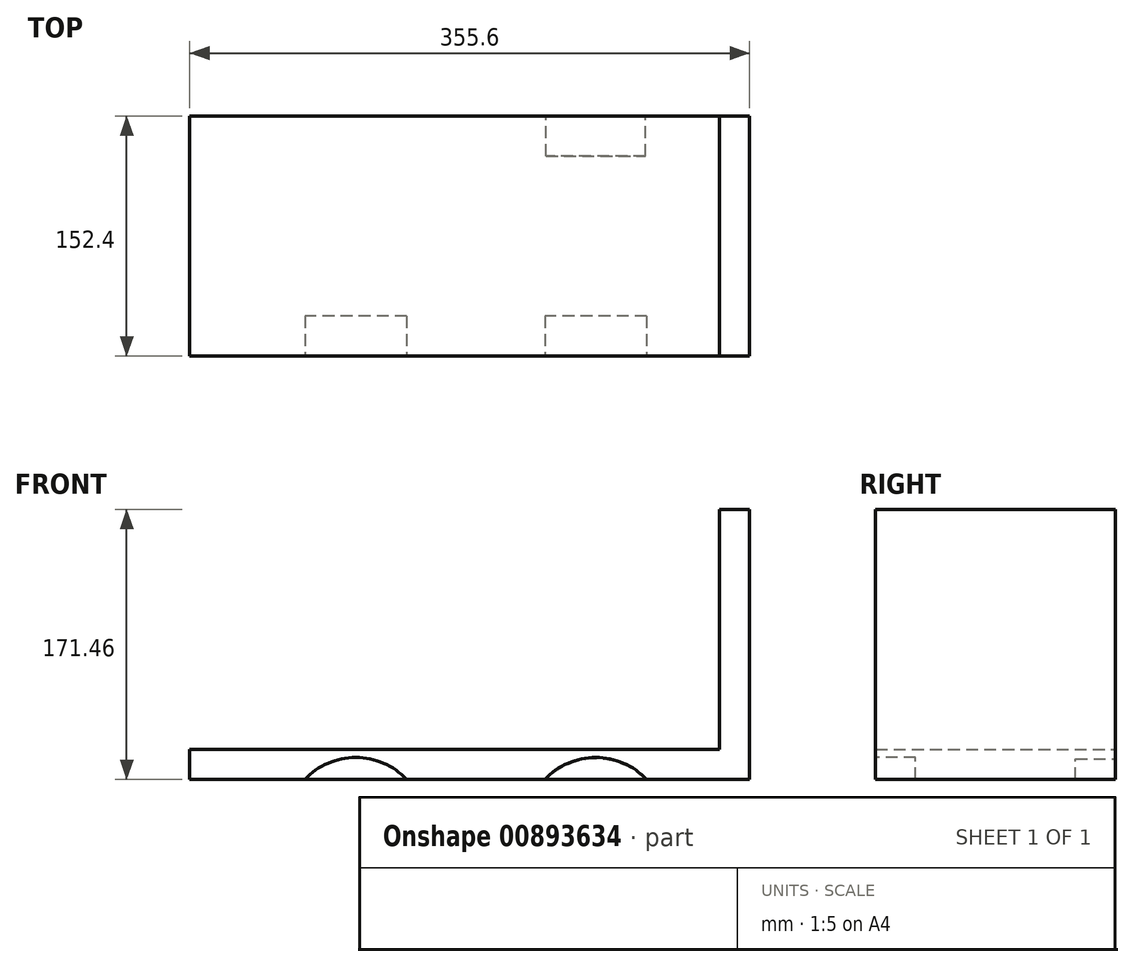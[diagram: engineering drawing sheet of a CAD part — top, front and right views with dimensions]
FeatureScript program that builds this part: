
annotation { "Feature Type Name" : "Feature", "Feature Type Description" : "" }
export const myFeature = defineFeature(function(context is Context, id is Id, definition is map)
    precondition{}
    {
        {
            var Q0;
            Q0=qCreatedBy(makeId("Front.planeOp"),FACE);
            var sketch = newSketch(context, id + "F0", { "sketchPlane" : qUnion([Q0])});
            skLineSegment(sketch, "E0.bottom", {"start": v(177.8, -9.52) * mm, "end": v(-177.8, -9.53) * mm});
            skLineSegment(sketch, "E0.top", {"start": v(177.8, 9.53) * mm, "end": v(-177.8, 9.53) * mm});
            skLineSegment(sketch, "E0.left", {"start": v(177.8, -9.52) * mm, "end": v(177.8, 9.53) * mm});
            skLineSegment(sketch, "E0.right", {"start": v(-177.8, -9.53) * mm, "end": v(-177.8, 9.53) * mm});
            skPoint(sketch, "E0.middle", {"position": v(0, 0) * mm});
            skPoint(sketch, "E1.middle", {"position": v(177.8, 9.53) * mm});
            skLineSegment(sketch, "E2", {"start": v(177.8, 9.53) * mm, "end": v(177.8, 161.93) * mm});
            skLineSegment(sketch, "E3", {"start": v(177.8, 161.93) * mm, "end": v(158.75, 161.93) * mm});
            skLineSegment(sketch, "E4", {"start": v(158.75, 161.93) * mm, "end": v(158.75, 9.53) * mm});
            skSolve(sketch);
        }
        {
            var Q0;
            Q0=makeQuery(id+"F0.imprint","IMPRINT",FACE,{"disambiguationData":[TD([[makeQuery(id+"F0.imprint","IMPRINT",EDGE,{"derivedFrom":sQuery(id+"F0.wireOp",EDGE,"E0.bottom")}),-1.0]])]});
            var Q1;
            {var subQ0=sQuery(id+"F0.wireOp",EDGE,"E2");Q1=makeQuery(id+"F0.imprint","IMPRINT",FACE,{"disambiguationData":[TD([[makeQuery(id+"F0.imprint","IMPRINT",EDGE,{"derivedFrom":subQ0}),1.0]])]});}
            extrude(context, id + "F1", {"entities" : qUnion([Q0, Q1]), "endBound" : BoundingType.SYMMETRIC, "depth" : 152.4 * mm, "offsetDistance" : 25.4 * mm});
        }
        {
            var Q0;
            Q0=makeQuery(id+"F1.opExtrude","CAP_FACE",FACE,{"disambiguationData":[OSD([sQuery(id+"F0.wireOp",EDGE,"E0.bottom"),sQuery(id+"F0.wireOp",EDGE,"E0.top"),sQuery(id+"F0.wireOp",EDGE,"E0.left"),sQuery(id+"F0.wireOp",EDGE,"E0.right"),sQuery(id+"F0.wireOp",EDGE,"E2"),sQuery(id+"F0.wireOp",EDGE,"E3"),sQuery(id+"F0.wireOp",EDGE,"E4")])],"isStart":false});
            var sketch = newSketch(context, id + "F2", { "sketchPlane" : qUnion([Q0])});
            skLineSegment(sketch, "E5", {"start": v(-177.8, -9.52) * mm, "end": v(-72.4, -9.52) * mm});
            skLineSegment(sketch, "E6", {"start": v(-72.39, -9.53) * mm, "end": v(-72.39, -40) * mm});
            skCircle(sketch, "E7", {"center": v(-72.39, -40) * mm, "radius": 44.45 * mm});
            skLineSegment(sketch, "E8", {"start": v(-72.4, -9.52) * mm, "end": v(80, -9.52) * mm});
            skLineSegment(sketch, "E9", {"start": v(80, -9.52) * mm, "end": v(80, -40) * mm});
            skCircle(sketch, "E10", {"center": v(80, -40) * mm, "radius": 44.45 * mm});
            skSolve(sketch);
        }
        {
            var Q0;
            {var subQ0=sQuery(id+"F2.wireOp",EDGE,"E5");var subQ1=makeQuery(id+"F1.opExtrude","CAP_EDGE",EDGE,{"disambiguationData":[OSD([sQuery(id+"F0.wireOp",EDGE,"E0.bottom")])],"isStart":false});var subQ2=makeQuery(id+"F2.imprint","INTERSECT",VERTEX,{"derivedFrom":[subQ1,subQ0]});Q0=makeQuery(id+"F2.imprint","IMPRINT",FACE,{"disambiguationData":[TD([[makeQuery(id+"F2.imprint","IMPRINT",EDGE,{"disambiguationData":[TD([[subQ2,-1.0]])],"derivedFrom":subQ0}),-1.0]])]});}
            var Q1;
            {var subQ0=sQuery(id+"F2.wireOp",EDGE,"E8");var subQ1=makeQuery(id+"F1.opExtrude","CAP_EDGE",EDGE,{"disambiguationData":[OSD([sQuery(id+"F0.wireOp",EDGE,"E0.bottom")])],"isStart":false});var subQ2=makeQuery(id+"F2.imprint","INTERSECT",VERTEX,{"derivedFrom":[subQ1,subQ0]});Q1=makeQuery(id+"F2.imprint","IMPRINT",FACE,{"disambiguationData":[TD([[makeQuery(id+"F2.imprint","IMPRINT",EDGE,{"disambiguationData":[TD([[subQ2,-1.0]])],"derivedFrom":subQ0}),-1.0]])]});}
            extrude(context, id + "F3", {"entities" : qUnion([Q0, Q1]), "operationType" : NewBodyOperationType.REMOVE, "oppositeDirection" : true, "depth" : 25.4 * mm, "offsetDistance" : 25.4 * mm});
        }
        {
            var Q0;
            Q0=makeQuery(id+"F1.opExtrude","CAP_FACE",FACE,{"disambiguationData":[OSD([sQuery(id+"F0.wireOp",EDGE,"E0.bottom"),sQuery(id+"F0.wireOp",EDGE,"E0.top"),sQuery(id+"F0.wireOp",EDGE,"E0.left"),sQuery(id+"F0.wireOp",EDGE,"E0.right"),sQuery(id+"F0.wireOp",EDGE,"E2"),sQuery(id+"F0.wireOp",EDGE,"E3"),sQuery(id+"F0.wireOp",EDGE,"E4")])],"isStart":true});
            var sketch = newSketch(context, id + "F4", { "sketchPlane" : qUnion([Q0])});
            skLineSegment(sketch, "E11", {"start": v(-80, -10.4) * mm, "end": v(-80, -40.87) * mm});
            skCircle(sketch, "E12", {"center": v(-80, -40.87) * mm, "radius": 44.45 * mm});
            skLineSegment(sketch, "E13", {"start": v(-80, -10.4) * mm, "end": v(72.4, -10.4) * mm});
            skLineSegment(sketch, "E14", {"start": v(72.4, -10.4) * mm, "end": v(72.4, -40.87) * mm});
            skCircle(sketch, "E15", {"center": v(72.4, -40.87) * mm, "radius": 44.45 * mm});
            skLineSegment(sketch, "E16", {"start": v(177.8, -9.53) * mm, "end": v(72.4, -10.4) * mm});
            skSolve(sketch);
        }
        {
            var Q0;
            {var subQ0=sQuery(id+"F4.wireOp",EDGE,"E12");var subQ1=makeQuery(id+"F1.opExtrude","CAP_EDGE",EDGE,{"disambiguationData":[OSD([sQuery(id+"F0.wireOp",EDGE,"E0.bottom")])],"isStart":true});var subQ2=makeQuery(id+"F4.imprint","INTERSECT",VERTEX,{"disambiguationData":[OD(0.0)],"derivedFrom":[subQ1,subQ0]});Q0=makeQuery(id+"F4.imprint","IMPRINT",FACE,{"disambiguationData":[TD([[makeQuery(id+"F4.imprint","IMPRINT",EDGE,{"disambiguationData":[TD([[subQ2,1.0]])],"derivedFrom":subQ0}),1.0]])]});}
            var Q1;
            {var subQ0=sQuery(id+"F4.wireOp",EDGE,"E15");var subQ1=makeQuery(id+"F1.opExtrude","CAP_EDGE",EDGE,{"disambiguationData":[OSD([sQuery(id+"F0.wireOp",EDGE,"E0.bottom")])],"isStart":true});var subQ2=makeQuery(id+"F4.imprint","INTERSECT",VERTEX,{"disambiguationData":[OD(0.0)],"derivedFrom":[subQ1,subQ0]});Q1=makeQuery(id+"F4.imprint","IMPRINT",FACE,{"disambiguationData":[TD([[makeQuery(id+"F4.imprint","IMPRINT",EDGE,{"disambiguationData":[TD([[subQ2,-1.0]])],"derivedFrom":subQ0}),1.0]])]});}
            extrude(context, id + "F5", {"entities" : qUnion([Q0, Q1]), "operationType" : NewBodyOperationType.REMOVE, "oppositeDirection" : true, "depth" : 25.4 * mm, "offsetDistance" : 25.4 * mm});
        }
    });
